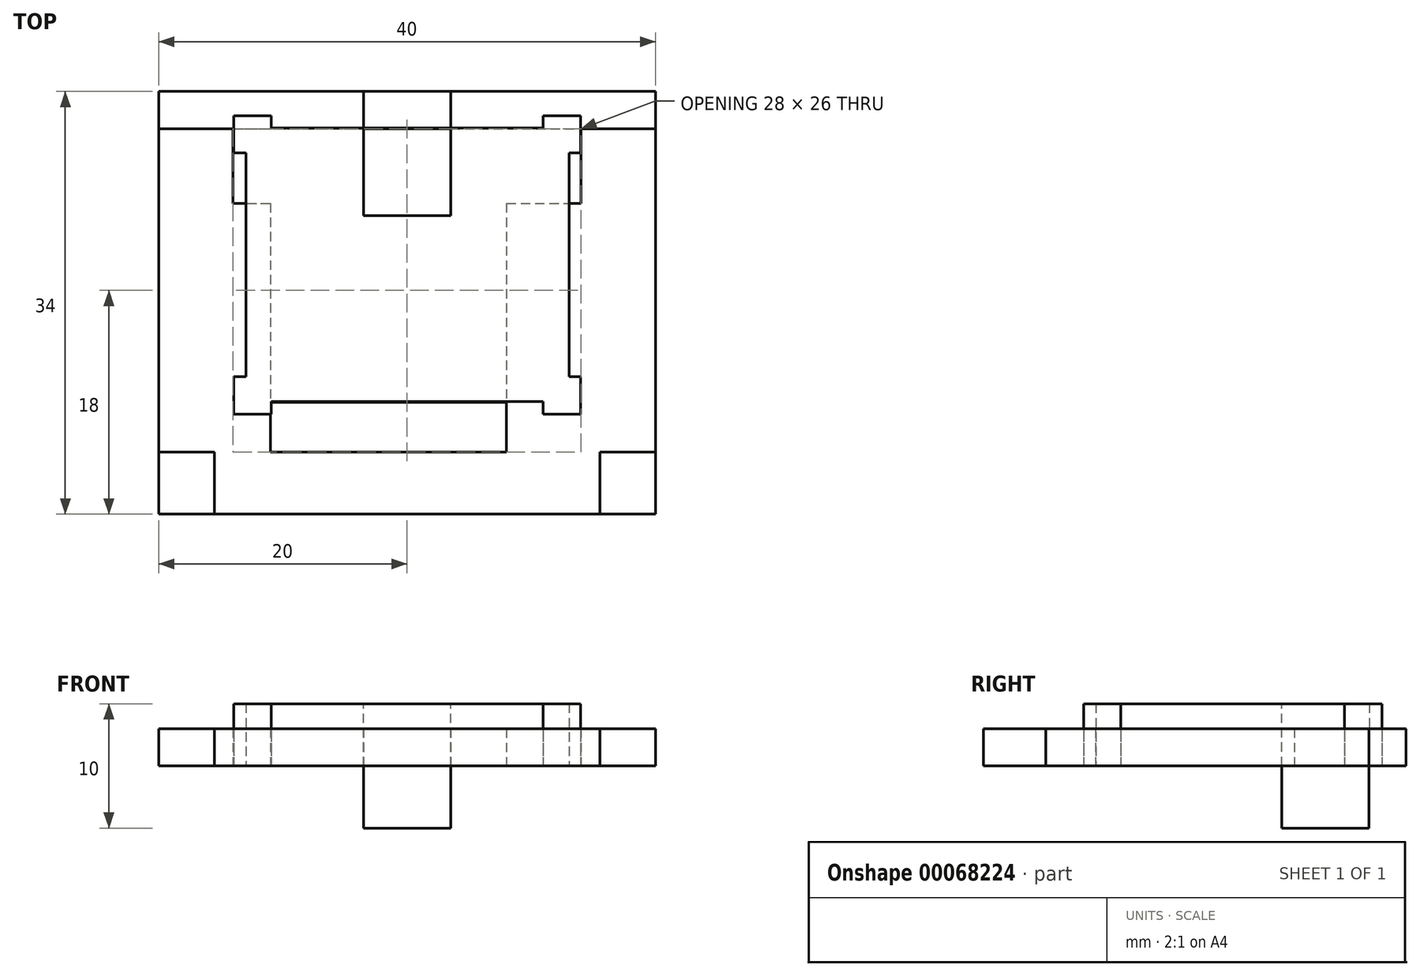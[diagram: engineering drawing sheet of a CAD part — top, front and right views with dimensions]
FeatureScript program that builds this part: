
annotation { "Feature Type Name" : "Feature", "Feature Type Description" : "" }
export const myFeature = defineFeature(function(context is Context, id is Id, definition is map)
    precondition{}
    {
        {
            var Q0;
            Q0=qCreatedBy(makeId("Top.planeOp"),FACE);
            var sketch = newSketch(context, id + "F0", { "sketchPlane" : qUnion([Q0])});
            skLineSegment(sketch, "E0.rect.bottom", {"start": v(-20, 17) * mm, "end": v(20, 17) * mm});
            skLineSegment(sketch, "E0.rect.top", {"start": v(-20, -17) * mm, "end": v(20, -17) * mm});
            skLineSegment(sketch, "E0.rect.left", {"start": v(-20, 17) * mm, "end": v(-20, -17) * mm});
            skLineSegment(sketch, "E0.rect.right", {"start": v(20, 17) * mm, "end": v(20, -17) * mm});
            skPoint(sketch, "E0.rect.middle", {"position": v(0, 0) * mm});
            skLineSegment(sketch, "E1.bottom", {"start": v(-20, -17) * mm, "end": v(-15.5, -17) * mm});
            skLineSegment(sketch, "E1.top", {"start": v(-20, -12) * mm, "end": v(-15.5, -12) * mm});
            skLineSegment(sketch, "E1.left", {"start": v(-20, -17) * mm, "end": v(-20, -12) * mm});
            skLineSegment(sketch, "E1.right", {"start": v(-15.5, -17) * mm, "end": v(-15.5, -12) * mm});
            skLineSegment(sketch, "E2.MirrorCS", {"start": v(15.5, -17) * mm, "end": v(15.5, -12) * mm});
            skLineSegment(sketch, "E3.MirrorCS", {"start": v(20, -17) * mm, "end": v(20, -12) * mm});
            skLineSegment(sketch, "E4.MirrorCS", {"start": v(20, -17) * mm, "end": v(15.5, -17) * mm});
            skLineSegment(sketch, "E5.MirrorCS", {"start": v(20, -12) * mm, "end": v(15.5, -12) * mm});
            skLineSegment(sketch, "E6.bottom", {"start": v(-20, 17) * mm, "end": v(-14, 17) * mm});
            skLineSegment(sketch, "E6.top", {"start": v(-20, 14) * mm, "end": v(-14, 14) * mm});
            skLineSegment(sketch, "E6.left", {"start": v(-20, 17) * mm, "end": v(-20, 14) * mm});
            skLineSegment(sketch, "E6.right", {"start": v(-14, 17) * mm, "end": v(-14, 14) * mm});
            skLineSegment(sketch, "E7.MirrorCS", {"start": v(20, 17) * mm, "end": v(20, 14) * mm});
            skLineSegment(sketch, "E8.MirrorCS", {"start": v(14, 17) * mm, "end": v(14, 14) * mm});
            skLineSegment(sketch, "E9.MirrorCS", {"start": v(20, 14) * mm, "end": v(14, 14) * mm});
            skLineSegment(sketch, "E10.MirrorCS", {"start": v(20, 17) * mm, "end": v(14, 17) * mm});
            skLineSegment(sketch, "E11.MirrorCS", {"start": v(20, 17) * mm, "end": v(-20, 17) * mm});
            skLineSegment(sketch, "E12.bottom", {"start": v(-14, 14) * mm, "end": v(14, 14) * mm});
            skLineSegment(sketch, "E12.top", {"start": v(-14, -12) * mm, "end": v(14, -12) * mm});
            skLineSegment(sketch, "E12.left", {"start": v(-14, 14) * mm, "end": v(-14, -12) * mm});
            skLineSegment(sketch, "E12.right", {"start": v(14, 14) * mm, "end": v(14, -12) * mm});
            skLineSegment(sketch, "E13.top", {"start": v(-14, 8) * mm, "end": v(14, 8) * mm});
            skLineSegment(sketch, "E13.left", {"start": v(-14, -12) * mm, "end": v(-14, 8) * mm});
            skLineSegment(sketch, "E13.right", {"start": v(14, -12) * mm, "end": v(14, 8) * mm});
            skLineSegment(sketch, "E14.bottom", {"start": v(-11, 8) * mm, "end": v(8, 8) * mm});
            skLineSegment(sketch, "E14.top", {"start": v(-11, -12) * mm, "end": v(8, -12) * mm});
            skLineSegment(sketch, "E14.left", {"start": v(-11, 8) * mm, "end": v(-11, -12) * mm});
            skLineSegment(sketch, "E14.right", {"start": v(8, 8) * mm, "end": v(8, -12) * mm});
            skLineSegment(sketch, "E15.bottom", {"start": v(0, 17) * mm, "end": v(-3.5, 17) * mm});
            skLineSegment(sketch, "E15.top", {"start": v(0, 7) * mm, "end": v(-3.5, 7) * mm});
            skLineSegment(sketch, "E15.left", {"start": v(0, 17) * mm, "end": v(0, 7) * mm});
            skLineSegment(sketch, "E15.right", {"start": v(-3.5, 17) * mm, "end": v(-3.5, 7) * mm});
            skLineSegment(sketch, "E16.MirrorCS", {"start": v(0, 17) * mm, "end": v(3.5, 17) * mm});
            skLineSegment(sketch, "E17.MirrorCS", {"start": v(3.5, 17) * mm, "end": v(3.5, 7) * mm});
            skLineSegment(sketch, "E18.MirrorCS", {"start": v(0, 7) * mm, "end": v(3.5, 7) * mm});
            skLineSegment(sketch, "E19.top", {"start": v(-14, -8) * mm, "end": v(14, -8) * mm});
            skLineSegment(sketch, "E19.left", {"start": v(-14, -12) * mm, "end": v(-14, -8) * mm});
            skLineSegment(sketch, "E19.right", {"start": v(14, -12) * mm, "end": v(14, -8) * mm});
            skSolve(sketch);
        }
        {
            var Q0;
            Q0=makeQuery(id+"F0.imprint","IMPRINT",FACE,{"disambiguationData":[TD([[makeQuery(id+"F0.imprint","IMPRINT",EDGE,{"derivedFrom":sQuery(id+"F0.wireOp",EDGE,"E6.top")}),1.0]])]});
            var Q1;
            {var subQ0=sQuery(id+"F0.wireOp",EDGE,"E6.right");Q1=makeQuery(id+"F0.imprint","IMPRINT",FACE,{"disambiguationData":[TD([[makeQuery(id+"F0.imprint","IMPRINT",EDGE,{"derivedFrom":subQ0}),1.0]])]});}
            var Q2;
            {var subQ0=sQuery(id+"F0.wireOp",EDGE,"E8.MirrorCS");Q2=makeQuery(id+"F0.imprint","IMPRINT",FACE,{"disambiguationData":[TD([[makeQuery(id+"F0.imprint","IMPRINT",EDGE,{"derivedFrom":subQ0}),-1.0]])]});}
            var Q3;
            {var subQ0=sQuery(id+"F0.wireOp",EDGE,"E8.MirrorCS");Q3=makeQuery(id+"F0.imprint","IMPRINT",FACE,{"disambiguationData":[TD([[makeQuery(id+"F0.imprint","IMPRINT",EDGE,{"derivedFrom":subQ0}),1.0]])]});}
            var Q4;
            Q4=makeQuery(id+"F0.imprint","IMPRINT",FACE,{"disambiguationData":[TD([[makeQuery(id+"F0.imprint","IMPRINT",EDGE,{"derivedFrom":sQuery(id+"F0.wireOp",EDGE,"E2.MirrorCS")}),-1.0]])]});
            var Q5;
            Q5=makeQuery(id+"F0.imprint","IMPRINT",FACE,{"disambiguationData":[TD([[makeQuery(id+"F0.imprint","IMPRINT",EDGE,{"derivedFrom":sQuery(id+"F0.wireOp",EDGE,"E0.rect.top")}),1.0]])]});
            var Q6;
            Q6=makeQuery(id+"F0.imprint","IMPRINT",FACE,{"disambiguationData":[TD([[makeQuery(id+"F0.imprint","IMPRINT",EDGE,{"derivedFrom":sQuery(id+"F0.wireOp",EDGE,"E1.bottom")}),1.0]])]});
            var Q7;
            {var subQ5=sQuery(id+"F0.wireOp",EDGE,"E19.left");Q7=makeQuery(id+"F0.imprint","IMPRINT",FACE,{"disambiguationData":[TD([[makeQuery(id+"F0.imprint","IMPRINT",EDGE,{"derivedFrom":subQ5}),-1.0]])]});}
            var Q8;
            {var subQ0=sQuery(id+"F0.wireOp",EDGE,"E12.top");var subQ1=sQuery(id+"F0.wireOp",EDGE,"E14.left");var subQ2=makeQuery(id+"F0.imprint","INTERSECT",VERTEX,{"derivedFrom":[subQ1,subQ0]});Q8=makeQuery(id+"F0.imprint","IMPRINT",FACE,{"disambiguationData":[TD([[makeQuery(id+"F0.imprint","IMPRINT",EDGE,{"disambiguationData":[TD([[subQ2,1.0]])],"derivedFrom":subQ1}),1.0]])]});}
            var Q9;
            {var subQ5=sQuery(id+"F0.wireOp",EDGE,"E19.right");Q9=makeQuery(id+"F0.imprint","IMPRINT",FACE,{"disambiguationData":[TD([[makeQuery(id+"F0.imprint","IMPRINT",EDGE,{"derivedFrom":subQ5}),1.0]])]});}
            extrude(context, id + "F1", {"entities" : qUnion([Q0, Q1, Q2, Q3, Q4, Q5, Q6, Q7, Q8, Q9]), "depth" : 3 * mm});
        }
        {
            var Q0;
            {var subQ5=sQuery(id+"F0.wireOp",EDGE,"E16.MirrorCS");Q0=makeQuery(id+"F0.imprint","IMPRINT",FACE,{"disambiguationData":[TD([[makeQuery(id+"F0.imprint","IMPRINT",EDGE,{"derivedFrom":subQ5}),-1.0]])]});}
            var Q1;
            {var subQ5=sQuery(id+"F0.wireOp",EDGE,"E15.bottom");Q1=makeQuery(id+"F0.imprint","IMPRINT",FACE,{"disambiguationData":[TD([[makeQuery(id+"F0.imprint","IMPRINT",EDGE,{"derivedFrom":subQ5}),1.0]])]});}
            var Q2;
            {var subQ0=sQuery(id+"F0.wireOp",EDGE,"E15.right");var subQ1=sQuery(id+"F0.wireOp",EDGE,"E12.bottom");var subQ2=makeQuery(id+"F0.imprint","INTERSECT",VERTEX,{"derivedFrom":[subQ1,subQ0]});Q2=makeQuery(id+"F0.imprint","IMPRINT",FACE,{"disambiguationData":[TD([[makeQuery(id+"F0.imprint","IMPRINT",EDGE,{"disambiguationData":[TD([[subQ2,-1.0]])],"derivedFrom":subQ1}),-1.0]])]});}
            var Q3;
            {var subQ0=sQuery(id+"F0.wireOp",EDGE,"E15.left");var subQ1=sQuery(id+"F0.wireOp",EDGE,"E12.bottom");var subQ2=makeQuery(id+"F0.imprint","INTERSECT",VERTEX,{"derivedFrom":[subQ1,subQ0]});Q3=makeQuery(id+"F0.imprint","IMPRINT",FACE,{"disambiguationData":[TD([[makeQuery(id+"F0.imprint","IMPRINT",EDGE,{"disambiguationData":[TD([[subQ2,-1.0]])],"derivedFrom":subQ1}),-1.0]])]});}
            var Q4;
            {var subQ5=sQuery(id+"F0.wireOp",EDGE,"E18.MirrorCS");Q4=makeQuery(id+"F0.imprint","IMPRINT",FACE,{"disambiguationData":[TD([[makeQuery(id+"F0.imprint","IMPRINT",EDGE,{"derivedFrom":subQ5}),1.0]])]});}
            var Q5;
            {var subQ5=sQuery(id+"F0.wireOp",EDGE,"E15.top");Q5=makeQuery(id+"F0.imprint","IMPRINT",FACE,{"disambiguationData":[TD([[makeQuery(id+"F0.imprint","IMPRINT",EDGE,{"derivedFrom":subQ5}),-1.0]])]});}
            extrude(context, id + "F2", {"entities" : qUnion([Q0, Q1, Q2, Q3, Q4, Q5]), "oppositeDirection" : true, "depth" : 5 * mm, "hasSecondDirection" : true, "secondDirectionOppositeDirection" : false, "secondDirectionDepth" : 5 * mm});
        }
        {
            var Q0;
            Q0=qCreatedBy(makeId("Top.planeOp"),FACE);
            var sketch = newSketch(context, id + "F3", { "sketchPlane" : qUnion([Q0])});
            skPoint(sketch, "E20.rect.middle", {"position": v(0.05, 16.44) * mm});
            skPoint(sketch, "E21.rect.middle", {"position": v(0, 0) * mm});
            skLineSegment(sketch, "E22", {"start": v(0.05, 14.05) * mm, "end": v(0.05, 18.82) * mm, "construction": true});
            skPoint(sketch, "E23", {"position": v(-56.83, 14.05) * mm});
            skPoint(sketch, "E24", {"position": v(56.93, 14.05) * mm});
            skLineSegment(sketch, "E25", {"start": v(-20.06, 17.02) * mm, "end": v(20.05, 17.02) * mm, "construction": true});
            skLineSegment(sketch, "E26.bottom", {"start": v(-12.95, 14.05) * mm, "end": v(13.05, 14.05) * mm});
            skLineSegment(sketch, "E26.top", {"start": v(-12.95, -7.95) * mm, "end": v(13.05, -7.95) * mm});
            skLineSegment(sketch, "E26.left", {"start": v(-12.95, 14.05) * mm, "end": v(-12.95, -7.95) * mm});
            skLineSegment(sketch, "E26.right", {"start": v(13.05, 14.05) * mm, "end": v(13.05, -7.95) * mm});
            skLineSegment(sketch, "E27", {"start": v(-22.7, 3.05) * mm, "end": v(13.05, 3.05) * mm, "construction": true});
            skLineSegment(sketch, "E28.bottom", {"start": v(-13.95, -5.95) * mm, "end": v(-10.95, -5.95) * mm});
            skLineSegment(sketch, "E28.top", {"start": v(-13.95, -8.95) * mm, "end": v(-10.95, -8.95) * mm});
            skLineSegment(sketch, "E28.left", {"start": v(-13.95, -5.95) * mm, "end": v(-13.95, -8.95) * mm});
            skLineSegment(sketch, "E28.right", {"start": v(-10.95, -5.95) * mm, "end": v(-10.95, -8.95) * mm});
            skLineSegment(sketch, "E29.bottom", {"start": v(-10.95, -7.95) * mm, "end": v(-12.95, -7.95) * mm});
            skLineSegment(sketch, "E29.top", {"start": v(-10.95, -5.95) * mm, "end": v(-12.95, -5.95) * mm});
            skLineSegment(sketch, "E29.left", {"start": v(-10.95, -7.95) * mm, "end": v(-10.95, -5.95) * mm});
            skLineSegment(sketch, "E29.right", {"start": v(-12.95, -7.95) * mm, "end": v(-12.95, -5.95) * mm});
            skPoint(sketch, "E30", {"position": v(0.05, 14.05) * mm});
            skLineSegment(sketch, "E31", {"start": v(0.05, 14.05) * mm, "end": v(0.05, -13.67) * mm, "construction": true});
            skPoint(sketch, "E31.endSnap0", {"position": v(0.05, -7.95) * mm});
            skLineSegment(sketch, "E32", {"start": v(0, 17.02) * mm, "end": v(0, -19.93) * mm, "construction": true});
            skLineSegment(sketch, "E33.MirrorCS", {"start": v(-0.06, 14.05) * mm, "end": v(-0.06, -13.67) * mm, "construction": true});
            skLineSegment(sketch, "E34.MirrorCS", {"start": v(10.94, -5.95) * mm, "end": v(12.94, -5.95) * mm});
            skLineSegment(sketch, "E35.MirrorCS", {"start": v(10.94, -7.95) * mm, "end": v(10.94, -5.95) * mm});
            skLineSegment(sketch, "E36.MirrorCS", {"start": v(10.94, -7.95) * mm, "end": v(12.94, -7.95) * mm});
            skLineSegment(sketch, "E37.MirrorCS", {"start": v(12.94, -7.95) * mm, "end": v(12.94, -5.95) * mm});
            skLineSegment(sketch, "E38.MirrorCS", {"start": v(-10.95, 12.05) * mm, "end": v(-12.95, 12.05) * mm});
            skLineSegment(sketch, "E39.MirrorCS", {"start": v(-10.95, 14.05) * mm, "end": v(-10.95, 12.05) * mm});
            skLineSegment(sketch, "E40.MirrorCS", {"start": v(-12.95, 14.05) * mm, "end": v(-12.95, 12.05) * mm});
            skLineSegment(sketch, "E41.MirrorCS", {"start": v(-10.95, 14.05) * mm, "end": v(-12.95, 14.05) * mm});
            skLineSegment(sketch, "E42.MirrorCS", {"start": v(10.94, 12.05) * mm, "end": v(12.94, 12.05) * mm});
            skLineSegment(sketch, "E43.MirrorCS", {"start": v(10.94, 14.05) * mm, "end": v(10.94, 12.05) * mm});
            skLineSegment(sketch, "E44.MirrorCS", {"start": v(10.94, 14.05) * mm, "end": v(12.94, 14.05) * mm});
            skLineSegment(sketch, "E45.MirrorCS", {"start": v(12.94, 14.05) * mm, "end": v(12.94, 12.05) * mm});
            skLineSegment(sketch, "E46.bottom", {"start": v(-10.95, 12.05) * mm, "end": v(-13.95, 12.05) * mm});
            skLineSegment(sketch, "E46.top", {"start": v(-10.95, 15.05) * mm, "end": v(-13.95, 15.05) * mm});
            skLineSegment(sketch, "E46.left", {"start": v(-10.95, 12.05) * mm, "end": v(-10.95, 15.05) * mm});
            skLineSegment(sketch, "E46.right", {"start": v(-13.95, 12.05) * mm, "end": v(-13.95, 15.05) * mm});
            skLineSegment(sketch, "E47.bottom", {"start": v(10.94, 12.05) * mm, "end": v(13.94, 12.05) * mm});
            skLineSegment(sketch, "E47.top", {"start": v(10.94, 15.05) * mm, "end": v(13.94, 15.05) * mm});
            skLineSegment(sketch, "E47.left", {"start": v(10.94, 12.05) * mm, "end": v(10.94, 15.05) * mm});
            skLineSegment(sketch, "E47.right", {"start": v(13.94, 12.05) * mm, "end": v(13.94, 15.05) * mm});
            skLineSegment(sketch, "E48.bottom", {"start": v(10.94, -5.95) * mm, "end": v(13.94, -5.95) * mm});
            skLineSegment(sketch, "E48.top", {"start": v(10.94, -8.95) * mm, "end": v(13.94, -8.95) * mm});
            skLineSegment(sketch, "E48.left", {"start": v(10.94, -5.95) * mm, "end": v(10.94, -8.95) * mm});
            skLineSegment(sketch, "E48.right", {"start": v(13.94, -5.95) * mm, "end": v(13.94, -8.95) * mm});
            skPoint(sketch, "E49", {"position": v(-0.06, 3.1) * mm});
            skLineSegment(sketch, "E50", {"start": v(-13.95, 15.05) * mm, "end": v(13.94, -8.95) * mm, "construction": true});
            skLineSegment(sketch, "E51", {"start": v(-13.95, -8.95) * mm, "end": v(13.94, 15.05) * mm, "construction": true});
            skSolve(sketch);
        }
        {
            var Q0;
            Q0 = qSketchRegion(id + "F0", true);
            var Q1;
            {var subQ5=sQuery(id+"F0.wireOp",EDGE,"E12.left");Q1=makeQuery(id+"F0.imprint","IMPRINT",FACE,{"disambiguationData":[TD([[makeQuery(id+"F0.imprint","IMPRINT",EDGE,{"derivedFrom":subQ5}),1.0]])]});}
            var Q2;
            {var subQ5=sQuery(id+"F0.wireOp",EDGE,"E12.right");Q2=makeQuery(id+"F0.imprint","IMPRINT",FACE,{"disambiguationData":[TD([[makeQuery(id+"F0.imprint","IMPRINT",EDGE,{"derivedFrom":subQ5}),-1.0]])]});}
            var Q3;
            {var subQ0=sQuery(id+"F0.wireOp",EDGE,"E13.right");Q3=makeQuery(id+"F0.imprint","IMPRINT",FACE,{"disambiguationData":[TD([[makeQuery(id+"F0.imprint","IMPRINT",EDGE,{"derivedFrom":subQ0}),1.0]])]});}
            var Q4;
            {var subQ0=sQuery(id+"F0.wireOp",EDGE,"E13.left");Q4=makeQuery(id+"F0.imprint","IMPRINT",FACE,{"disambiguationData":[TD([[makeQuery(id+"F0.imprint","IMPRINT",EDGE,{"derivedFrom":subQ0}),-1.0]])]});}
            extrude(context, id + "F4", {"entities" : qUnion([Q0, Q1, Q2, Q3, Q4]), "depth" : 3 * mm});
        }
        {
            var Q0;
            Q0 = qSketchRegion(id + "F3", true);
            var Q1;
            Q1=makeQuery(id+"F3.imprint","IMPRINT",FACE,{"disambiguationData":[TD([[makeQuery(id+"F3.imprint","IMPRINT",EDGE,{"derivedFrom":sQuery(id+"F3.wireOp",EDGE,"E21.rect.bottom")}),-1.0]])]});
            extrude(context, id + "F5", {"entities" : qUnion([Q0, Q1]), "depth" : 5 * mm});
        }
    });
